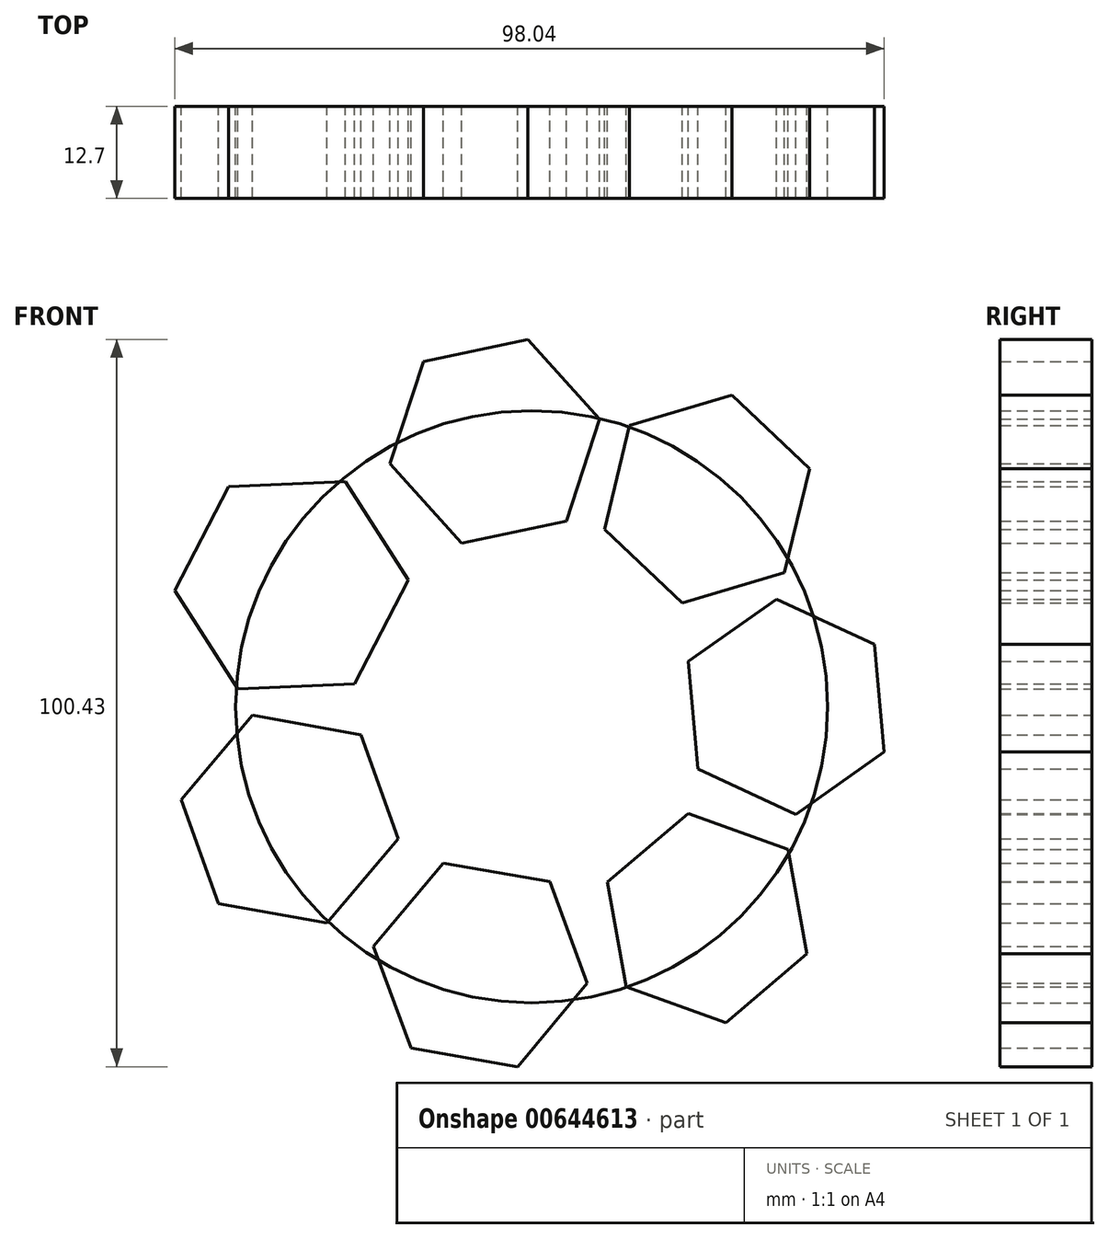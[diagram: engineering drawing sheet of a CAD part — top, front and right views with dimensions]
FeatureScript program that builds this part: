
annotation { "Feature Type Name" : "Feature", "Feature Type Description" : "" }
export const myFeature = defineFeature(function(context is Context, id is Id, definition is map)
    precondition{}
    {
        {
            var Q0;
            Q0=qCreatedBy(makeId("Front.planeOp"),FACE);
            var sketch = newSketch(context, id + "F0", { "sketchPlane" : qUnion([Q0])});
            skCircle(sketch, "E0", {"center": v(0, 0) * mm, "radius": 40.9 * mm});
            skSolve(sketch);
        }
        {
            var Q0;
            Q0=qCreatedBy(makeId("Front.planeOp"),FACE);
            var sketch = newSketch(context, id + "F1", { "sketchPlane" : qUnion([Q0])});
            skCircle(sketch, "E1.cCircle", {"center": v(-5.1, 36.65) * mm, "radius": 12.8 * mm, "construction": true});
            skLineSegment(sketch, "E1.0", {"start": v(9.38, 39.7) * mm, "end": v(4.79, 25.65) * mm});
            skLineSegment(sketch, "E1.1", {"start": v(4.79, 25.65) * mm, "end": v(-9.68, 22.6) * mm});
            skLineSegment(sketch, "E1.2", {"start": v(-9.68, 22.6) * mm, "end": v(-19.56, 33.6) * mm});
            skLineSegment(sketch, "E1.3", {"start": v(-19.56, 33.6) * mm, "end": v(-14.97, 47.66) * mm});
            skLineSegment(sketch, "E1.4", {"start": v(-14.97, 47.66) * mm, "end": v(-0.5, 50.7) * mm});
            skLineSegment(sketch, "E1.5", {"start": v(-0.5, 50.7) * mm, "end": v(9.38, 39.7) * mm});
            skPoint(sketch, "E1.0.midPoint", {"position": v(7.08, 32.67) * mm});
            skSolve(sketch);
        }
        {
            var Q0;
            Q0=qCreatedBy(makeId("Front.planeOp"),FACE);
            var sketch = newSketch(context, id + "F2", { "sketchPlane" : qUnion([Q0])});
            skCircle(sketch, "E2.cCircle", {"center": v(-33.17, 16.77) * mm, "radius": 14 * mm, "construction": true});
            skLineSegment(sketch, "E2.0", {"start": v(-17.02, 17.48) * mm, "end": v(-24.48, 3.14) * mm});
            skLineSegment(sketch, "E2.1", {"start": v(-24.48, 3.14) * mm, "end": v(-40.63, 2.43) * mm});
            skLineSegment(sketch, "E2.2", {"start": v(-40.63, 2.43) * mm, "end": v(-49.33, 16.06) * mm});
            skLineSegment(sketch, "E2.3", {"start": v(-49.33, 16.06) * mm, "end": v(-41.87, 30.4) * mm});
            skLineSegment(sketch, "E2.4", {"start": v(-41.87, 30.4) * mm, "end": v(-25.71, 31.12) * mm});
            skLineSegment(sketch, "E2.5", {"start": v(-25.71, 31.12) * mm, "end": v(-17.02, 17.48) * mm});
            skPoint(sketch, "E2.0.midPoint", {"position": v(-20.75, 10.31) * mm});
            skSolve(sketch);
        }
        {
            var Q0;
            Q0=qCreatedBy(makeId("Front.planeOp"),FACE);
            var sketch = newSketch(context, id + "F3", { "sketchPlane" : qUnion([Q0])});
            skCircle(sketch, "E3.cCircle", {"center": v(-33.42, -15.53) * mm, "radius": 13.2 * mm, "construction": true});
            skLineSegment(sketch, "E3.0", {"start": v(-43.26, -27.18) * mm, "end": v(-48.43, -12.83) * mm});
            skLineSegment(sketch, "E3.1", {"start": v(-48.43, -12.83) * mm, "end": v(-38.58, -1.18) * mm});
            skLineSegment(sketch, "E3.2", {"start": v(-38.58, -1.18) * mm, "end": v(-23.58, -3.88) * mm});
            skLineSegment(sketch, "E3.3", {"start": v(-23.58, -3.88) * mm, "end": v(-18.41, -18.23) * mm});
            skLineSegment(sketch, "E3.4", {"start": v(-18.41, -18.23) * mm, "end": v(-28.26, -29.88) * mm});
            skLineSegment(sketch, "E3.5", {"start": v(-28.26, -29.88) * mm, "end": v(-43.26, -27.18) * mm});
            skPoint(sketch, "E3.0.midPoint", {"position": v(-45.84, -20) * mm});
            skSolve(sketch);
        }
        {
            var Q0;
            Q0=qCreatedBy(makeId("Front.planeOp"),FACE);
            var sketch = newSketch(context, id + "F4", { "sketchPlane" : qUnion([Q0])});
            skCircle(sketch, "E4.cCircle", {"center": v(-7.08, -35.66) * mm, "radius": 12.97 * mm, "construction": true});
            skLineSegment(sketch, "E4.0", {"start": v(-16.67, -47.16) * mm, "end": v(-21.84, -33.1) * mm});
            skLineSegment(sketch, "E4.1", {"start": v(-21.84, -33.1) * mm, "end": v(-12.25, -21.6) * mm});
            skLineSegment(sketch, "E4.2", {"start": v(-12.25, -21.6) * mm, "end": v(2.51, -24.15) * mm});
            skLineSegment(sketch, "E4.3", {"start": v(2.51, -24.15) * mm, "end": v(7.68, -38.21) * mm});
            skLineSegment(sketch, "E4.4", {"start": v(7.68, -38.21) * mm, "end": v(-1.92, -49.72) * mm});
            skLineSegment(sketch, "E4.5", {"start": v(-1.92, -49.72) * mm, "end": v(-16.67, -47.16) * mm});
            skPoint(sketch, "E4.0.midPoint", {"position": v(-19.26, -40.13) * mm});
            skSolve(sketch);
        }
        {
            var Q0;
            Q0=qCreatedBy(makeId("Front.planeOp"),FACE);
            var sketch = newSketch(context, id + "F5", { "sketchPlane" : qUnion([Q0])});
            skCircle(sketch, "E5.cCircle", {"center": v(24.23, -29.2) * mm, "radius": 12.7 * mm, "construction": true});
            skLineSegment(sketch, "E5.0", {"start": v(38.02, -34.15) * mm, "end": v(26.83, -43.62) * mm});
            skLineSegment(sketch, "E5.1", {"start": v(26.83, -43.62) * mm, "end": v(13.04, -38.66) * mm});
            skLineSegment(sketch, "E5.2", {"start": v(13.04, -38.66) * mm, "end": v(10.43, -24.24) * mm});
            skLineSegment(sketch, "E5.3", {"start": v(10.43, -24.24) * mm, "end": v(21.62, -14.77) * mm});
            skLineSegment(sketch, "E5.4", {"start": v(21.62, -14.77) * mm, "end": v(35.42, -19.73) * mm});
            skLineSegment(sketch, "E5.5", {"start": v(35.42, -19.73) * mm, "end": v(38.02, -34.15) * mm});
            skPoint(sketch, "E5.0.midPoint", {"position": v(32.43, -38.89) * mm});
            skSolve(sketch);
        }
        {
            var Q0;
            Q0=qCreatedBy(makeId("Front.planeOp"),FACE);
            var sketch = newSketch(context, id + "F6", { "sketchPlane" : qUnion([Q0])});
            skCircle(sketch, "E6.cCircle", {"center": v(35.16, 0) * mm, "radius": 12.93 * mm, "construction": true});
            skLineSegment(sketch, "E6.0", {"start": v(48.71, -6.26) * mm, "end": v(36.52, -14.86) * mm});
            skLineSegment(sketch, "E6.1", {"start": v(36.52, -14.86) * mm, "end": v(22.97, -8.6) * mm});
            skLineSegment(sketch, "E6.2", {"start": v(22.97, -8.6) * mm, "end": v(21.6, 6.26) * mm});
            skLineSegment(sketch, "E6.3", {"start": v(21.6, 6.26) * mm, "end": v(33.8, 14.86) * mm});
            skLineSegment(sketch, "E6.4", {"start": v(33.8, 14.86) * mm, "end": v(47.35, 8.6) * mm});
            skLineSegment(sketch, "E6.5", {"start": v(47.35, 8.6) * mm, "end": v(48.71, -6.26) * mm});
            skPoint(sketch, "E6.0.midPoint", {"position": v(42.61, -10.56) * mm});
            skSolve(sketch);
        }
        {
            var Q0;
            Q0=qCreatedBy(makeId("Front.planeOp"),FACE);
            var sketch = newSketch(context, id + "F7", { "sketchPlane" : qUnion([Q0])});
            skCircle(sketch, "E7.cCircle", {"center": v(24.23, 28.7) * mm, "radius": 12.78 * mm, "construction": true});
            skLineSegment(sketch, "E7.0", {"start": v(38.37, 32.9) * mm, "end": v(34.93, 18.54) * mm});
            skLineSegment(sketch, "E7.1", {"start": v(34.93, 18.54) * mm, "end": v(20.78, 14.35) * mm});
            skLineSegment(sketch, "E7.2", {"start": v(20.78, 14.35) * mm, "end": v(10.08, 24.5) * mm});
            skLineSegment(sketch, "E7.3", {"start": v(10.08, 24.5) * mm, "end": v(13.52, 38.85) * mm});
            skLineSegment(sketch, "E7.4", {"start": v(13.52, 38.85) * mm, "end": v(27.67, 43.05) * mm});
            skLineSegment(sketch, "E7.5", {"start": v(27.67, 43.05) * mm, "end": v(38.37, 32.9) * mm});
            skPoint(sketch, "E7.0.midPoint", {"position": v(36.65, 25.72) * mm});
            skSolve(sketch);
        }
        {
            var Q0;
            Q0 = qSketchRegion(id + "F7", true);
            var Q1;
            Q1 = qSketchRegion(id + "F6", true);
            var Q2;
            Q2 = qSketchRegion(id + "F5", true);
            var Q3;
            Q3 = qSketchRegion(id + "F4", true);
            var Q4;
            Q4 = qSketchRegion(id + "F3", true);
            var Q5;
            Q5 = qSketchRegion(id + "F1", true);
            var Q6;
            Q6 = qSketchRegion(id + "F2", true);
            var Q7;
            Q7 = qSketchRegion(id + "F0", true);
            extrude(context, id + "F8", {"entities" : qUnion([Q0, Q1, Q2, Q3, Q4, Q5, Q6, Q7]), "depth" : 12.7 * mm, "offsetDistance" : 25.4 * mm});
        }
    });
